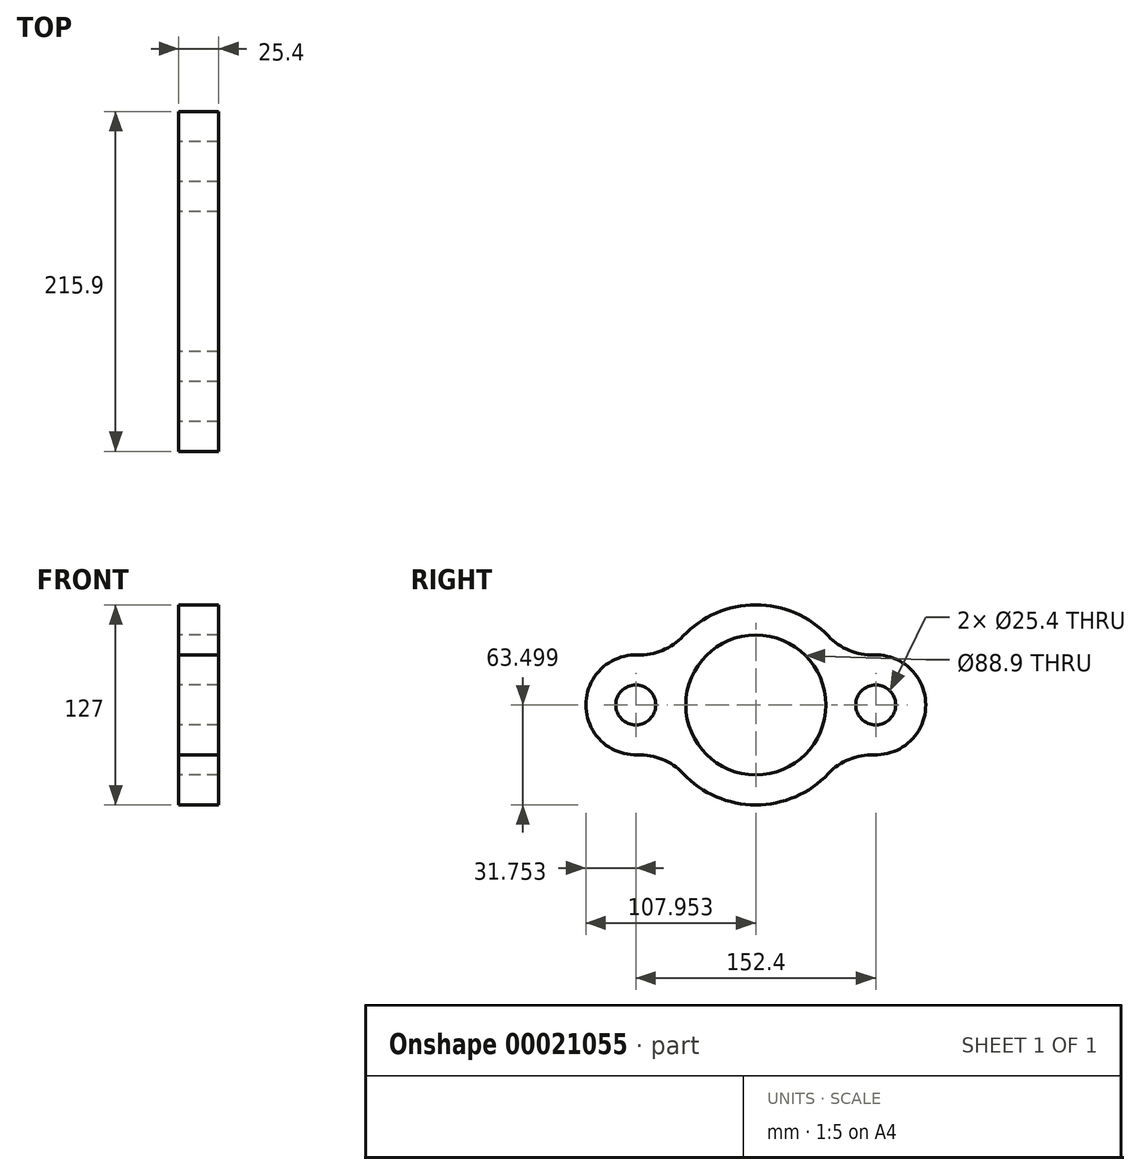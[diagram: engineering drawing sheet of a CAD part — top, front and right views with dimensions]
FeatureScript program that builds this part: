
annotation { "Feature Type Name" : "Feature", "Feature Type Description" : "" }
export const myFeature = defineFeature(function(context is Context, id is Id, definition is map)
    precondition{}
    {
        {
            var Q0;
            Q0=qCreatedBy(makeId("Right.planeOp"),FACE);
            var sketch = newSketch(context, id + "F0", { "sketchPlane" : qUnion([Q0])});
            skCircle(sketch, "E0", {"center": v(-35.5, 41.34) * mm, "radius": 44.45 * mm});
            skArc(sketch, "E1", {"start": v(10.64, 84.97) * mm, "mid": v(-35.5, 104.84) * mm, "end": v(-81.63, 84.97) * mm});
            skCircle(sketch, "E2", {"center": v(-111.7, 41.34) * mm, "radius": 12.7 * mm});
            skCircle(sketch, "E3", {"center": v(40.7, 41.34) * mm, "radius": 12.7 * mm});
            skArc(sketch, "E4", {"start": v(-110.61, 73.07) * mm, "mid": v(-143.45, 41.34) * mm, "end": v(-110.61, 9.6) * mm});
            skArc(sketch, "E5", {"start": v(39.62, 9.6) * mm, "mid": v(72.45, 41.34) * mm, "end": v(39.62, 73.07) * mm});
            skPoint(sketch, "E6.visualSharp", {"position": v(22.45, 67.31) * mm});
            skArc(sketch, "E6.filletArc", {"start": v(10.64, 84.97) * mm, "mid": v(23.85, 75.9) * mm, "end": v(39.62, 73.07) * mm});
            skArc(sketch, "E7.trimOffspring", {"start": v(-81.63, -2.3) * mm, "mid": v(-35.5, -22.16) * mm, "end": v(10.64, -2.3) * mm});
            skPoint(sketch, "E8.visualSharp", {"position": v(-93.44, 67.31) * mm});
            skArc(sketch, "E8.filletArc", {"start": v(-110.61, 73.07) * mm, "mid": v(-94.84, 75.9) * mm, "end": v(-81.63, 84.97) * mm});
            skPoint(sketch, "E9.visualSharp", {"position": v(-93.44, 15.36) * mm});
            skArc(sketch, "E9.filletArc", {"start": v(-81.63, -2.3) * mm, "mid": v(-94.84, 6.77) * mm, "end": v(-110.61, 9.6) * mm});
            skPoint(sketch, "E10.visualSharp", {"position": v(22.45, 15.36) * mm});
            skArc(sketch, "E10.filletArc", {"start": v(39.62, 9.6) * mm, "mid": v(23.85, 6.77) * mm, "end": v(10.64, -2.3) * mm});
            skPoint(sketch, "E11.0", {"position": v(0, 0) * mm});
            skSolve(sketch);
        }
        {
            var Q0;
            Q0=makeQuery(id+"F0.imprint","IMPRINT",FACE,{"disambiguationData":[TD([[makeQuery(id+"F0.imprint","IMPRINT",EDGE,{"derivedFrom":sQuery(id+"F0.wireOp",EDGE,"E0")}),-1.0]])]});
            extrude(context, id + "F1", {"entities" : qUnion([Q0]), "depth" : 25.4 * mm});
        }
    });
